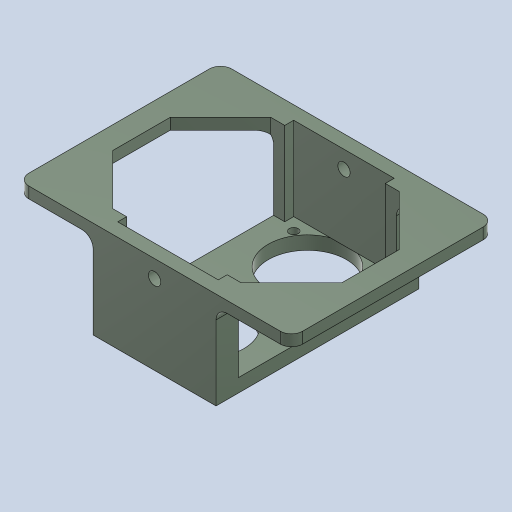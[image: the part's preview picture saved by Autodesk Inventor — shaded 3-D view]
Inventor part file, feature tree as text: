
AUTODESK INVENTOR PART (.ipt)
format: ipt  version: 2023 (Build 270158000, 158)  size: 298,496 bytes
history: native  units: mm
features: sketch x8, extrude x7, projected_geometry x3, hole x2, fillet x2, other x1, mirror x1, chamfer x1
ambient origin geometry x8: Origin, YZ Plane, XZ Plane, XY Plane, X Axis, Y Axis, Z Axis, Center Point
bodies: Body1 (feature_tree)
feature tree (25):
  other  "ソリッド1"
  extrude  "押し出し1"  Depth=31.5mm
  sketch  "スケッチ2"
  extrude  "押し出し2"  Depth=22.0mm
  extrude  "押し出し3"  Depth=14.0mm
  extrude  "押し出し5"  Depth=2.4mm TaperAngle=0.0deg
  hole  "穴1"  [1 undecoded]
  extrude  "補強"  Depth=8.5mm
  mirror  "ミラー2"
  extrude  "穴抜き"  Depth=2.0mm
  chamfer  "面取り1"  Distance=49.0mm
  fillet  "フィレット1"  Radius=2.0mm
  hole  "穴2"  [1 undecoded]
  extrude  "押し出し10"  Depth=1.6mm
  fillet  "フィレット2"  Radius=14.0mm
  sketch  "スケッチ1"
  projected_geometry  "投影ループ1"
  sketch  "スケッチ3"
  sketch  "スケッチ5"
  sketch  "スケッチ6"
  sketch  "スケッチ7"
  sketch  "スケッチ10"
  sketch  "スケッチ11"
  projected_geometry  "投影ループ2"
  projected_geometry  "投影ループ3"
note: 2 required parameter values undecoded (feature->parameter linkage not recoverable at this tier; creation-order binding heuristic only, values carry confidence <= 0.55)
